# Revit family: Shades-Hunter_Douglas-RB500-Single_Standard_Duty-Auto-Bracket_Block_Out-3in-tw77-ky
name_source: partatom
category: Specialty Equipment
units: mm (PartAtom-declared; Revit-internal decimal feet)

## family parameters
Always vertical = Yes
Cut with Voids When Loaded = No
OmniClass Number = 23.30.60.14
OmniClass Title = Interior Window Treatment
Part Type = Normal
Room Calculation Point = No
Round Connector Dimension = Use Diameter
Shared = No
Work Plane-Based = No

## types (1)
- Automated
    Assembly Code = E2010300
    CD_Bracket Depth = 0' - 3 5/32"
    CD_Bracket Height = 0' - 3 5/16"
    CD_Fabric Sizing Disclaimer = Designer to verify maximum fabric size with Manufacturer as the maximum fabric size is dependent on finished dimensions
    CD_Finish = Fabric-Shade-Hunter_Douglas-5%-E_Screen-Charcoal_Cocoa
    CD_Finish Frame = Metal-Aluminum-Hunter_Douglas-Anodized-White
    CD_Finish Rail = Metal-Aluminum-Hunter_Douglas-Anodized-White
    CD_Install Documentation = https://www.hunterdouglasarchitectural.com
    CD_Microsite = https://microsite.caddetails.com
    CD_Product Documentation Link = https://www.hunterdouglasarchitectural.com
    CD_Product Name = RB 500 Roller Shade System
    CD_Product Page URL = https://www.hunterdouglasarchitectural.com
    CD_Warranty = https://assets.hunterdouglasarchitectural.com
    Description = Standard Duty Automated Roller Shade
    Manufacturer = Hunter Douglas Architectural
    Model = Standard Duty Automated 3IN Bracket Block Out
    Type Comments = Block Out Shade
    URL = https://www.hunterdouglasarchitectural.com

## geometry (parser evidence)
native form markers: Sweep x2
no freeform markers — native parametric forms only
